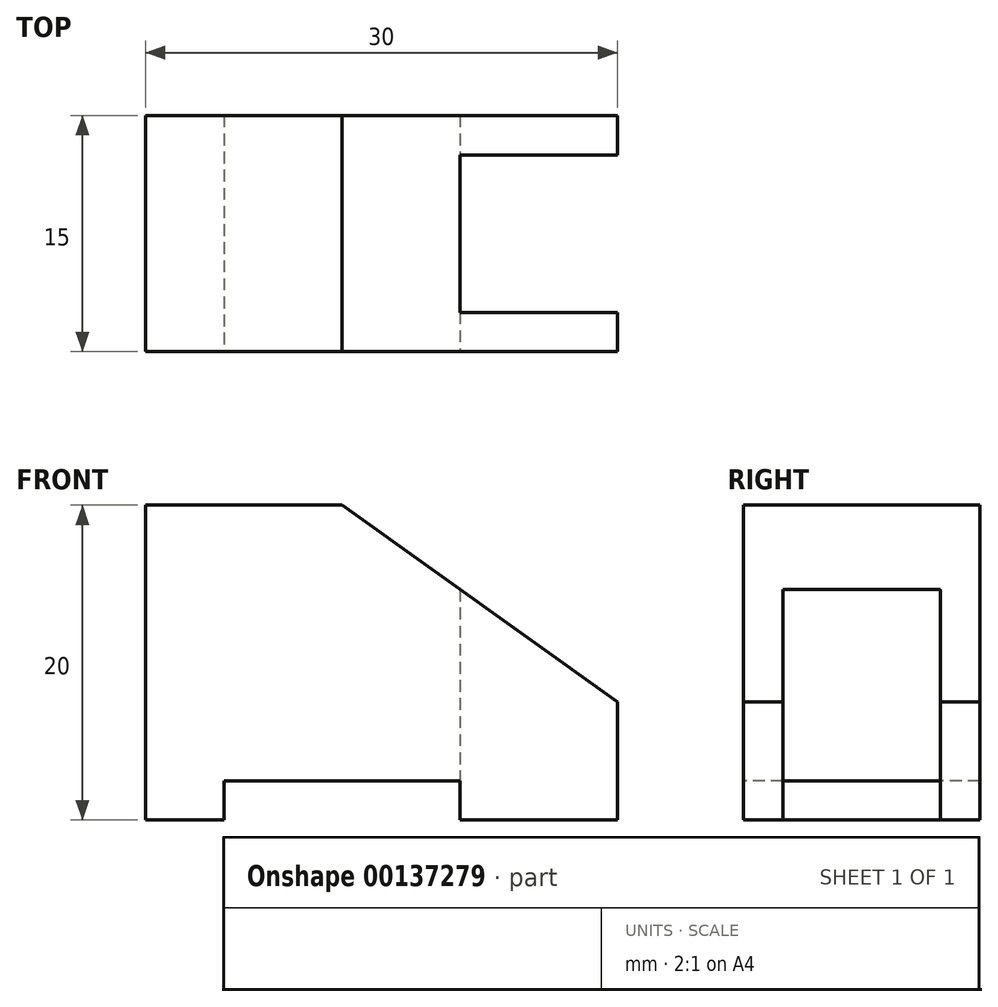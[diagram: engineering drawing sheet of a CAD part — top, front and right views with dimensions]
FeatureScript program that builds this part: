
annotation { "Feature Type Name" : "Feature", "Feature Type Description" : "" }
export const myFeature = defineFeature(function(context is Context, id is Id, definition is map)
    precondition{}
    {
        {
            var Q0;
            Q0=qCreatedBy(makeId("Top.planeOp"),FACE);
            var sketch = newSketch(context, id + "F0", { "sketchPlane" : qUnion([Q0])});
            skLineSegment(sketch, "E0", {"start": v(0, 0) * mm, "end": v(0, 15) * mm});
            skLineSegment(sketch, "E1", {"start": v(0, 15) * mm, "end": v(30, 15) * mm});
            skLineSegment(sketch, "E2", {"start": v(30, 15) * mm, "end": v(30, 12.5) * mm});
            skLineSegment(sketch, "E3", {"start": v(30, 12.5) * mm, "end": v(20, 12.5) * mm});
            skLineSegment(sketch, "E4", {"start": v(20, 12.5) * mm, "end": v(20, 2.5) * mm});
            skLineSegment(sketch, "E5", {"start": v(20, 2.5) * mm, "end": v(30, 2.5) * mm});
            skLineSegment(sketch, "E6", {"start": v(30, 2.5) * mm, "end": v(30, 0) * mm});
            skLineSegment(sketch, "E7", {"start": v(30, 0) * mm, "end": v(0, 0) * mm});
            skLineSegment(sketch, "E8", {"start": v(12.5, 15) * mm, "end": v(12.5, 0) * mm});
            skSolve(sketch);
        }
        {
            var Q0;
            {var subQ0=sQuery(id+"F0.wireOp",EDGE,"E0");Q0=makeQuery(id+"F0.imprint","IMPRINT",FACE,{"disambiguationData":[TD([[makeQuery(id+"F0.imprint","IMPRINT",EDGE,{"derivedFrom":subQ0}),-1.0]])]});}
            var Q1;
            {var subQ0=sQuery(id+"F0.wireOp",EDGE,"E2");Q1=makeQuery(id+"F0.imprint","IMPRINT",FACE,{"disambiguationData":[TD([[makeQuery(id+"F0.imprint","IMPRINT",EDGE,{"derivedFrom":subQ0}),-1.0]])]});}
            extrude(context, id + "F1", {"entities" : qUnion([Q0, Q1]), "depth" : 20 * mm});
        }
        {
            var Q0;
            Q0=makeQuery(id+"F1.opExtrude","SWEPT_FACE",FACE,{"disambiguationData":[OSD([sQuery(id+"F0.wireOp",EDGE,"E7")])]});
            var sketch = newSketch(context, id + "F2", { "sketchPlane" : qUnion([Q0])});
            skLineSegment(sketch, "E9", {"start": v(12.5, 20) * mm, "end": v(30, 7.5) * mm});
            skLineSegment(sketch, "E10", {"start": v(30, 7.5) * mm, "end": v(30, 20) * mm});
            skLineSegment(sketch, "E11", {"start": v(30, 20) * mm, "end": v(12.5, 20) * mm});
            skLineSegment(sketch, "E12", {"start": v(5, 0) * mm, "end": v(5, 2.5) * mm});
            skLineSegment(sketch, "E13", {"start": v(5, 2.5) * mm, "end": v(20, 2.5) * mm});
            skLineSegment(sketch, "E14", {"start": v(20, 2.5) * mm, "end": v(20, 0) * mm});
            skSolve(sketch);
        }
        {
            var Q0;
            Q0=makeQuery(id+"F2.imprint","IMPRINT",FACE,{"disambiguationData":[TD([[makeQuery(id+"F2.imprint","IMPRINT",EDGE,{"derivedFrom":sQuery(id+"F2.wireOp",EDGE,"E9")}),1.0]])]});
            var Q1;
            {var subQ0=sQuery(id+"F2.wireOp",EDGE,"E12");Q1=makeQuery(id+"F2.imprint","IMPRINT",FACE,{"disambiguationData":[TD([[makeQuery(id+"F2.imprint","IMPRINT",EDGE,{"derivedFrom":subQ0}),-1.0]])]});}
            extrude(context, id + "F3", {"entities" : qUnion([Q0, Q1]), "operationType" : NewBodyOperationType.REMOVE, "endBound" : BoundingType.THROUGH_ALL, "oppositeDirection" : true, "depth" : 25 * mm});
        }
    });
